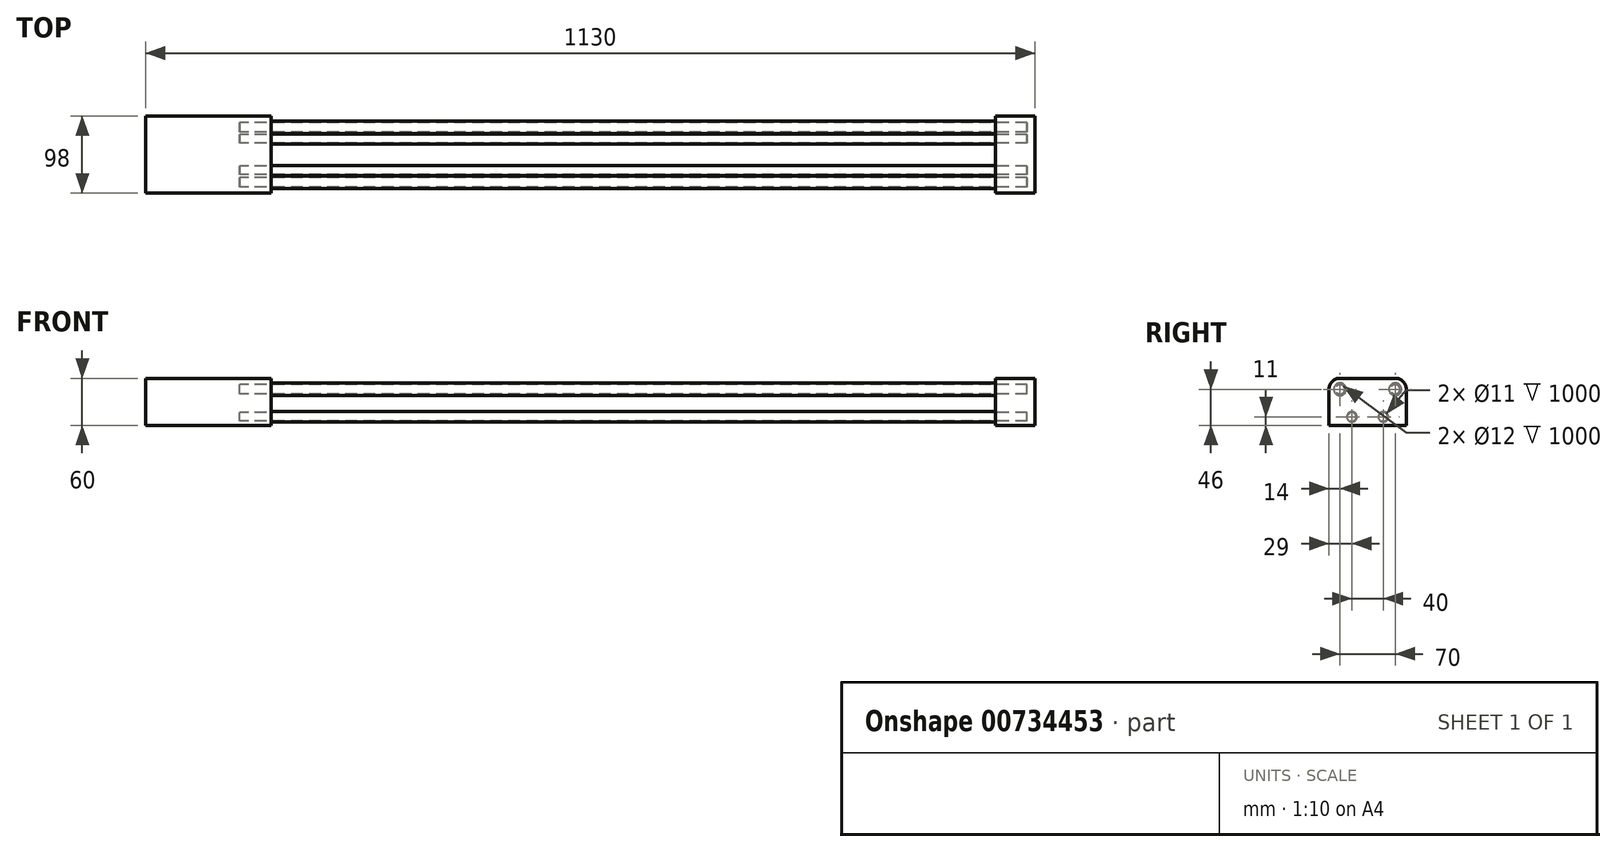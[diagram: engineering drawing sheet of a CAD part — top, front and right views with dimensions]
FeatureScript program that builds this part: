
annotation { "Feature Type Name" : "Feature", "Feature Type Description" : "" }
export const myFeature = defineFeature(function(context is Context, id is Id, definition is map)
    precondition{}
    {
        {
            var Q0;
            Q0=qCreatedBy(makeId("Right.planeOp"),FACE);
            var sketch = newSketch(context, id + "F0", { "sketchPlane" : qUnion([Q0])});
            skCircle(sketch, "E0", {"center": v(35, 0) * mm, "radius": 8 * mm});
            skCircle(sketch, "E1", {"center": v(-35, 0) * mm, "radius": 8 * mm});
            skCircle(sketch, "E2", {"center": v(-35, 0) * mm, "radius": 6 * mm});
            skCircle(sketch, "E3", {"center": v(35, 0) * mm, "radius": 6 * mm});
            skCircle(sketch, "E4", {"center": v(-20, -35) * mm, "radius": 6.5 * mm});
            skCircle(sketch, "E5", {"center": v(20, -35) * mm, "radius": 6.5 * mm});
            skCircle(sketch, "E6", {"center": v(-20, -35) * mm, "radius": 5.5 * mm});
            skCircle(sketch, "E7", {"center": v(20, -35) * mm, "radius": 5.5 * mm});
            skSolve(sketch);
        }
        {
            var Q0;
            Q0=qSketchRegion(id+"F0",true);
            extrude(context, id + "F1", {"entities" : qUnion([Q0]), "depth" : 500 * mm, "offsetDistance" : 25 * mm, "hasSecondDirection" : true, "secondDirectionOppositeDirection" : true, "secondDirectionDepth" : 500 * mm});
        }
        {
            var Q0;
            Q0=makeQuery(id+"F1.opExtrude","CAP_FACE",FACE,{"disambiguationData":[OSD([sQuery(id+"F0.wireOp",EDGE,"E0"),sQuery(id+"F0.wireOp",EDGE,"E3")])],"isStart":false});
            var sketch = newSketch(context, id + "F2", { "sketchPlane" : qUnion([Q0])});
            skLineSegment(sketch, "E8.bottom", {"start": v(-49, 14) * mm, "end": v(49, 14) * mm});
            skLineSegment(sketch, "E8.top", {"start": v(-49, -46) * mm, "end": v(49, -46) * mm});
            skLineSegment(sketch, "E8.left", {"start": v(-49, 14) * mm, "end": v(-49, -46) * mm});
            skLineSegment(sketch, "E8.right", {"start": v(49, 14) * mm, "end": v(49, -46) * mm});
            skPoint(sketch, "E8.middle", {"position": v(0, -16) * mm});
            skCircle(sketch, "E9.0", {"center": v(-35, 0) * mm, "radius": 8 * mm});
            skCircle(sketch, "E10.0", {"center": v(-20, -35) * mm, "radius": 6.5 * mm});
            skCircle(sketch, "E11.0", {"center": v(20, -35) * mm, "radius": 6.5 * mm});
            skCircle(sketch, "E12.0", {"center": v(35, 0) * mm, "radius": 8 * mm});
            skSolve(sketch);
        }
        {
            var Q0;
            Q0=makeQuery(id+"F2.imprint","IMPRINT",FACE,{"disambiguationData":[TD([[makeQuery(id+"F2.imprint","IMPRINT",EDGE,{"derivedFrom":sQuery(id+"F2.wireOp",EDGE,"E8.bottom")}),-1.0]])]});
            extrude(context, id + "F3", {"entities" : qUnion([Q0]), "oppositeDirection" : true, "depth" : 40 * mm, "offsetDistance" : 25 * mm});
        }
        {
            var Q0;
            Q0=makeQuery(id+"F3.opExtrude","CAP_FACE",FACE,{"disambiguationData":[OSD([sQuery(id+"F2.wireOp",EDGE,"E8.bottom"),sQuery(id+"F2.wireOp",EDGE,"E8.top"),sQuery(id+"F2.wireOp",EDGE,"E8.left"),sQuery(id+"F2.wireOp",EDGE,"E8.right"),sQuery(id+"F2.wireOp",EDGE,"E9.0"),sQuery(id+"F2.wireOp",EDGE,"E10.0"),sQuery(id+"F2.wireOp",EDGE,"E11.0"),sQuery(id+"F2.wireOp",EDGE,"E12.0")])],"isStart":true});
            var sketch = newSketch(context, id + "F4", { "sketchPlane" : qUnion([Q0])});
            skLineSegment(sketch, "E13.0.0", {"start": v(-49, 14) * mm, "end": v(-49, -46) * mm});
            skLineSegment(sketch, "E13.0.1", {"start": v(-49, -46) * mm, "end": v(49, -46) * mm});
            skLineSegment(sketch, "E13.0.2", {"start": v(49, -46) * mm, "end": v(49, 14) * mm});
            skLineSegment(sketch, "E13.0.3", {"start": v(49, 14) * mm, "end": v(-49, 14) * mm});
            skSolve(sketch);
        }
        {
            var Q0;
            Q0=qSketchRegion(id+"F4",true);
            extrude(context, id + "F5", {"entities" : qUnion([Q0]), "operationType" : NewBodyOperationType.ADD, "depth" : 10 * mm, "offsetDistance" : 25 * mm});
        }
        {
            var Q0;
            Q0=makeQuery(id+"F5.boolean.opBoolean","MERGE",EDGE,{"derivedFrom":[makeQuery(id+"F3.opExtrude","SWEPT_EDGE",EDGE,{"disambiguationData":[OSD([sQuery(id+"F2.wireOp",EDGE,"E8.bottom"),sQuery(id+"F2.wireOp",EDGE,"E8.left")])]}),makeQuery(id+"F5.opExtrude","SWEPT_EDGE",EDGE,{"disambiguationData":[OSD([sQuery(id+"F4.wireOp",EDGE,"E13.0.0"),sQuery(id+"F4.wireOp",EDGE,"E13.0.3")])]})]});
            var Q1;
            Q1=makeQuery(id+"F5.boolean.opBoolean","MERGE",EDGE,{"derivedFrom":[makeQuery(id+"F3.opExtrude","SWEPT_EDGE",EDGE,{"disambiguationData":[OSD([sQuery(id+"F2.wireOp",EDGE,"E8.bottom"),sQuery(id+"F2.wireOp",EDGE,"E8.right")])]}),makeQuery(id+"F5.opExtrude","SWEPT_EDGE",EDGE,{"disambiguationData":[OSD([sQuery(id+"F4.wireOp",EDGE,"E13.0.2"),sQuery(id+"F4.wireOp",EDGE,"E13.0.3")])]})]});
            fillet(context, id + "F6", {"entities" : qUnion([Q0, Q1]), "radius" : 14 * mm, "tangentPropagation" : true, "allowEdgeOverflow" : false});
        }
        {
            var Q0;
            Q0=makeQuery(id+"F1.opExtrude","CAP_FACE",FACE,{"disambiguationData":[OSD([sQuery(id+"F0.wireOp",EDGE,"E0"),sQuery(id+"F0.wireOp",EDGE,"E3")])],"isStart":true});
            var sketch = newSketch(context, id + "F7", { "sketchPlane" : qUnion([Q0])});
            skLineSegment(sketch, "E14.0.0", {"start": v(35, 14) * mm, "end": v(-35, 14) * mm});
            skArc(sketch, "E14.0.1", {"start": v(-35, 14) * mm, "mid": v(-44.9, 9.9) * mm, "end": v(-49, 0) * mm});
            skLineSegment(sketch, "E14.0.2", {"start": v(-49, 0) * mm, "end": v(-49, -46) * mm});
            skLineSegment(sketch, "E14.0.3", {"start": v(-49, -46) * mm, "end": v(49, -46) * mm});
            skLineSegment(sketch, "E14.0.4", {"start": v(49, -46) * mm, "end": v(49, 0) * mm});
            skArc(sketch, "E14.0.5", {"start": v(49, 0) * mm, "mid": v(44.9, 9.9) * mm, "end": v(35, 14) * mm});
            skCircle(sketch, "E15.0", {"center": v(-35, 0) * mm, "radius": 8 * mm});
            skCircle(sketch, "E16.0", {"center": v(35, 0) * mm, "radius": 8 * mm});
            skCircle(sketch, "E17.0", {"center": v(20, -35) * mm, "radius": 6.5 * mm});
            skCircle(sketch, "E18.0", {"center": v(-20, -35) * mm, "radius": 6.5 * mm});
            skSolve(sketch);
        }
        {
            var Q0;
            Q0=qSketchRegion(id+"F7",true);
            extrude(context, id + "F8", {"entities" : qUnion([Q0]), "oppositeDirection" : true, "depth" : 40 * mm, "offsetDistance" : 25 * mm});
        }
        {
            var Q0;
            Q0=makeQuery(id+"F8.opExtrude","CAP_FACE",FACE,{"disambiguationData":[OSD([sQuery(id+"F7.wireOp",EDGE,"E14.0.0"),sQuery(id+"F7.wireOp",EDGE,"E14.0.1"),sQuery(id+"F7.wireOp",EDGE,"E14.0.2"),sQuery(id+"F7.wireOp",EDGE,"E14.0.3"),sQuery(id+"F7.wireOp",EDGE,"E14.0.4"),sQuery(id+"F7.wireOp",EDGE,"E14.0.5"),sQuery(id+"F7.wireOp",EDGE,"E15.0"),sQuery(id+"F7.wireOp",EDGE,"E16.0"),sQuery(id+"F7.wireOp",EDGE,"E17.0"),sQuery(id+"F7.wireOp",EDGE,"E18.0")])],"isStart":true});
            var sketch = newSketch(context, id + "F9", { "sketchPlane" : qUnion([Q0])});
            skLineSegment(sketch, "E19.0.0", {"start": v(49, -46) * mm, "end": v(49, 0) * mm});
            skArc(sketch, "E19.0.1", {"start": v(49, 0) * mm, "mid": v(44.9, 9.9) * mm, "end": v(35, 14) * mm});
            skLineSegment(sketch, "E19.0.2", {"start": v(35, 14) * mm, "end": v(-35, 14) * mm});
            skArc(sketch, "E19.0.3", {"start": v(-35, 14) * mm, "mid": v(-44.9, 9.9) * mm, "end": v(-49, 0) * mm});
            skLineSegment(sketch, "E19.0.4", {"start": v(-49, 0) * mm, "end": v(-49, -46) * mm});
            skLineSegment(sketch, "E19.0.5", {"start": v(-49, -46) * mm, "end": v(49, -46) * mm});
            skSolve(sketch);
        }
        {
            var Q0;
            Q0=qSketchRegion(id+"F9",true);
            extrude(context, id + "F10", {"entities" : qUnion([Q0]), "operationType" : NewBodyOperationType.ADD, "depth" : 120 * mm, "offsetDistance" : 25 * mm});
        }
    });
